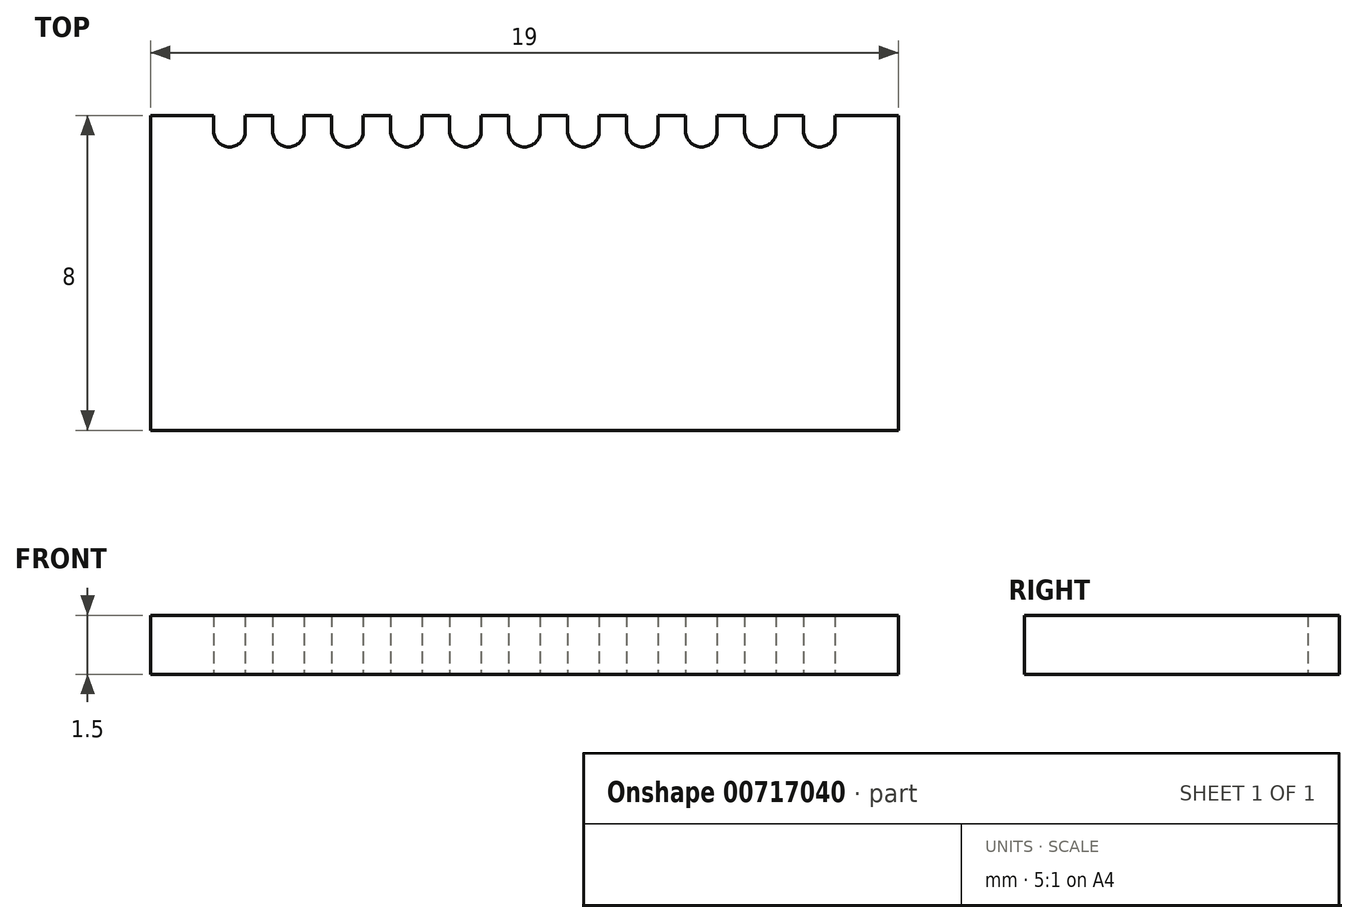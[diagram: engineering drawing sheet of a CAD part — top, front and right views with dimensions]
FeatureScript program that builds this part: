
annotation { "Feature Type Name" : "Feature", "Feature Type Description" : "" }
export const myFeature = defineFeature(function(context is Context, id is Id, definition is map)
    precondition{}
    {
        {
            var Q0;
            Q0=qCreatedBy(makeId("Top.planeOp"),FACE);
            var sketch = newSketch(context, id + "F0", { "sketchPlane" : qUnion([Q0])});
            skLineSegment(sketch, "E0.bottom", {"start": v(-9.5, 4) * mm, "end": v(9.5, 4) * mm});
            skLineSegment(sketch, "E0.top", {"start": v(-9.5, -4) * mm, "end": v(9.5, -4) * mm});
            skLineSegment(sketch, "E0.left", {"start": v(-9.5, 4) * mm, "end": v(-9.5, -4) * mm});
            skLineSegment(sketch, "E0.right", {"start": v(9.5, 4) * mm, "end": v(9.5, -4) * mm});
            skCircle(sketch, "E1", {"center": v(-7.5, 3.6) * mm, "radius": 0.4 * mm});
            skLineSegment(sketch, "E2", {"start": v(-7.9, 3.6) * mm, "end": v(-7.9, 4) * mm});
            skLineSegment(sketch, "E3", {"start": v(-7.1, 3.6) * mm, "end": v(-7.1, 4) * mm});
            skCircle(sketch, "E4.1.0.0", {"center": v(-6, 3.6) * mm, "radius": 0.4 * mm});
            skLineSegment(sketch, "E4.1.0.1", {"start": v(-6.4, 3.6) * mm, "end": v(-6.4, 4) * mm});
            skLineSegment(sketch, "E4.1.0.2", {"start": v(-5.6, 3.6) * mm, "end": v(-5.6, 4) * mm});
            skCircle(sketch, "E4.2.0.0", {"center": v(-4.5, 3.6) * mm, "radius": 0.4 * mm});
            skLineSegment(sketch, "E4.2.0.1", {"start": v(-4.9, 3.6) * mm, "end": v(-4.9, 4) * mm});
            skLineSegment(sketch, "E4.2.0.2", {"start": v(-4.1, 3.6) * mm, "end": v(-4.1, 4) * mm});
            skCircle(sketch, "E4.3.0.0", {"center": v(-3, 3.6) * mm, "radius": 0.4 * mm});
            skLineSegment(sketch, "E4.3.0.1", {"start": v(-3.4, 3.6) * mm, "end": v(-3.4, 4) * mm});
            skLineSegment(sketch, "E4.3.0.2", {"start": v(-2.6, 3.6) * mm, "end": v(-2.6, 4) * mm});
            skCircle(sketch, "E4.4.0.0", {"center": v(-1.5, 3.6) * mm, "radius": 0.4 * mm});
            skLineSegment(sketch, "E4.4.0.1", {"start": v(-1.9, 3.6) * mm, "end": v(-1.9, 4) * mm});
            skLineSegment(sketch, "E4.4.0.2", {"start": v(-1.1, 3.6) * mm, "end": v(-1.1, 4) * mm});
            skCircle(sketch, "E4.5.0.0", {"center": v(0, 3.6) * mm, "radius": 0.4 * mm});
            skLineSegment(sketch, "E4.5.0.1", {"start": v(-0.4, 3.6) * mm, "end": v(-0.4, 4) * mm});
            skLineSegment(sketch, "E4.5.0.2", {"start": v(0.4, 3.6) * mm, "end": v(0.4, 4) * mm});
            skCircle(sketch, "E4.6.0.0", {"center": v(1.5, 3.6) * mm, "radius": 0.4 * mm});
            skLineSegment(sketch, "E4.6.0.1", {"start": v(1.1, 3.6) * mm, "end": v(1.1, 4) * mm});
            skLineSegment(sketch, "E4.6.0.2", {"start": v(1.9, 3.6) * mm, "end": v(1.9, 4) * mm});
            skCircle(sketch, "E4.7.0.0", {"center": v(3, 3.6) * mm, "radius": 0.4 * mm});
            skLineSegment(sketch, "E4.7.0.1", {"start": v(2.6, 3.6) * mm, "end": v(2.6, 4) * mm});
            skLineSegment(sketch, "E4.7.0.2", {"start": v(3.4, 3.6) * mm, "end": v(3.4, 4) * mm});
            skCircle(sketch, "E4.8.0.0", {"center": v(4.5, 3.6) * mm, "radius": 0.4 * mm});
            skLineSegment(sketch, "E4.8.0.1", {"start": v(4.1, 3.6) * mm, "end": v(4.1, 4) * mm});
            skLineSegment(sketch, "E4.8.0.2", {"start": v(4.9, 3.6) * mm, "end": v(4.9, 4) * mm});
            skCircle(sketch, "E4.9.0.0", {"center": v(6, 3.6) * mm, "radius": 0.4 * mm});
            skLineSegment(sketch, "E4.9.0.1", {"start": v(5.6, 3.6) * mm, "end": v(5.6, 4) * mm});
            skLineSegment(sketch, "E4.9.0.2", {"start": v(6.4, 3.6) * mm, "end": v(6.4, 4) * mm});
            skCircle(sketch, "E4.10.0.0", {"center": v(7.5, 3.6) * mm, "radius": 0.4 * mm});
            skLineSegment(sketch, "E4.10.0.1", {"start": v(7.1, 3.6) * mm, "end": v(7.1, 4) * mm});
            skLineSegment(sketch, "E4.10.0.2", {"start": v(7.9, 3.6) * mm, "end": v(7.9, 4) * mm});
            skLineSegment(sketch, "E4.direction1", {"start": v(-7.9, 3.6) * mm, "end": v(-6.4, 3.6) * mm, "construction": true});
            skSolve(sketch);
        }
        {
            var Q0;
            Q0=makeQuery(id+"F0.imprint","IMPRINT",FACE,{"disambiguationData":[TD([[makeQuery(id+"F0.imprint","IMPRINT",EDGE,{"derivedFrom":sQuery(id+"F0.wireOp",EDGE,"E0.bottom")}),-1.0]])]});
            extrude(context, id + "F1", {"entities" : qUnion([Q0]), "depth" : 1.5 * mm, "offsetDistance" : 25 * mm});
        }
    });
